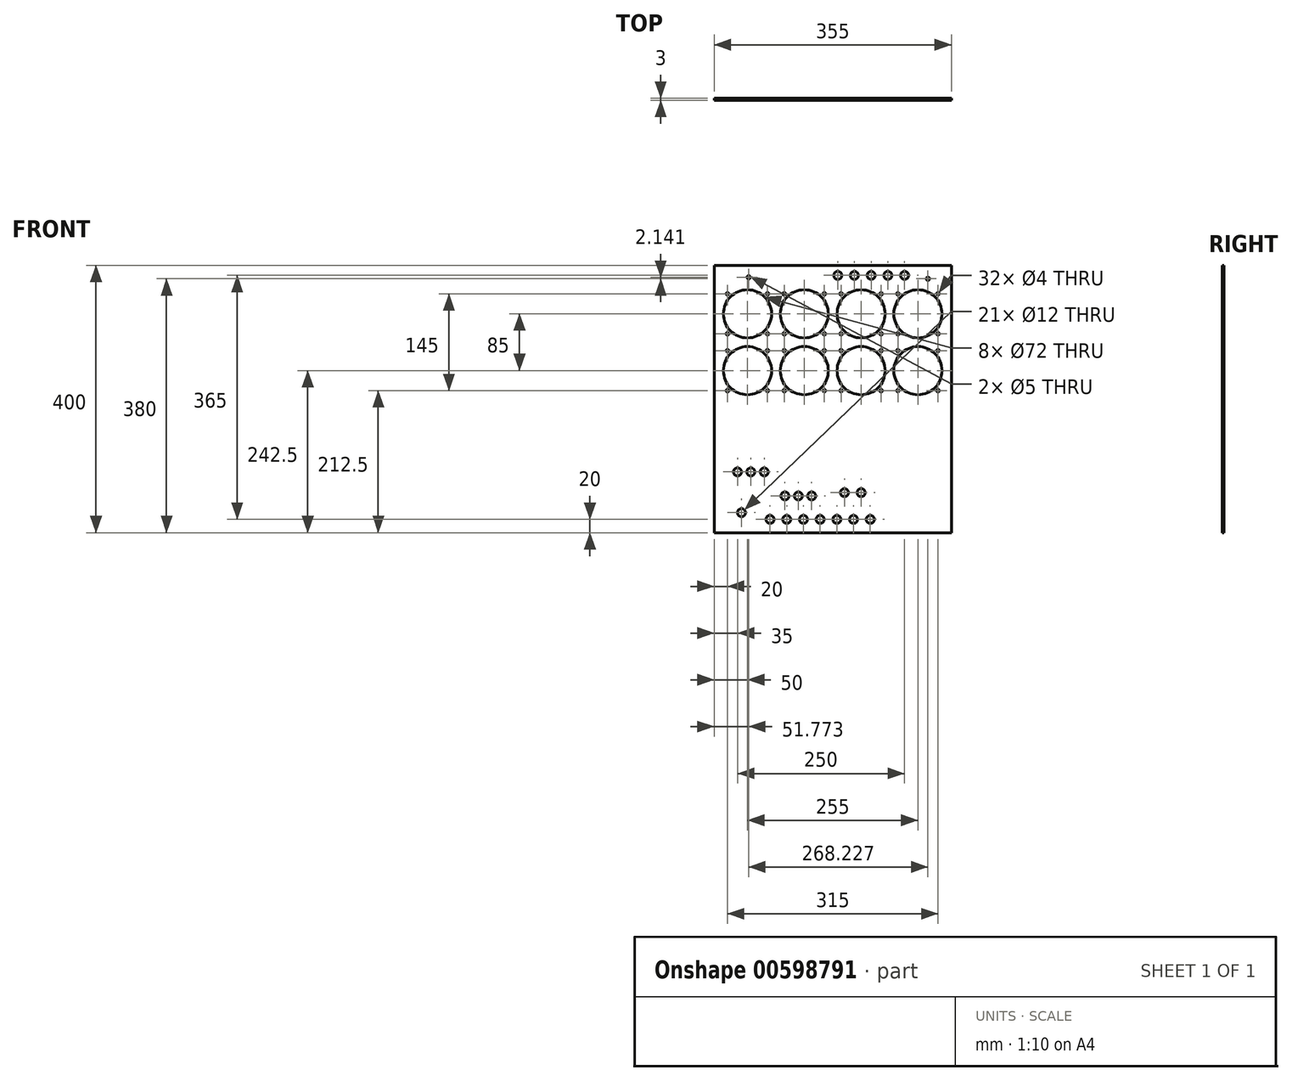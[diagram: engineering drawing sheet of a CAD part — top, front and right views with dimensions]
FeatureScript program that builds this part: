
annotation { "Feature Type Name" : "Feature", "Feature Type Description" : "" }
export const myFeature = defineFeature(function(context is Context, id is Id, definition is map)
    precondition{}
    {
        {
            var Q0;
            Q0=qCreatedBy(makeId("Front.planeOp"),FACE);
            var sketch = newSketch(context, id + "F0", { "sketchPlane" : qUnion([Q0])});
            skLineSegment(sketch, "E0.bottom", {"start": v(0, 0) * mm, "end": v(355, 0) * mm});
            skLineSegment(sketch, "E0.top", {"start": v(0, 400) * mm, "end": v(355, 400) * mm});
            skLineSegment(sketch, "E0.left", {"start": v(0, 0) * mm, "end": v(0, 400) * mm});
            skLineSegment(sketch, "E0.right", {"start": v(355, 0) * mm, "end": v(355, 400) * mm});
            skCircle(sketch, "E1", {"center": v(50, 327.5) * mm, "radius": 36 * mm});
            skCircle(sketch, "E2.0.1.0", {"center": v(50, 242.5) * mm, "radius": 36 * mm});
            skCircle(sketch, "E2.1.0.0", {"center": v(135, 327.5) * mm, "radius": 36 * mm});
            skCircle(sketch, "E2.1.1.0", {"center": v(135, 242.5) * mm, "radius": 36 * mm});
            skCircle(sketch, "E2.2.0.0", {"center": v(220, 327.5) * mm, "radius": 36 * mm});
            skCircle(sketch, "E2.2.1.0", {"center": v(220, 242.5) * mm, "radius": 36 * mm});
            skCircle(sketch, "E2.3.0.0", {"center": v(305, 327.5) * mm, "radius": 36 * mm});
            skCircle(sketch, "E2.3.1.0", {"center": v(305, 242.5) * mm, "radius": 36 * mm});
            skLineSegment(sketch, "E2.direction1", {"start": v(50, 327.5) * mm, "end": v(135, 327.5) * mm, "construction": true});
            skLineSegment(sketch, "E2.direction2", {"start": v(50, 327.5) * mm, "end": v(50, 242.5) * mm, "construction": true});
            skSolve(sketch);
        }
        {
            var Q0;
            Q0 = qSketchRegion(id + "F0", true);
            var Q1;
            Q1=makeQuery(id+"F0.imprint","IMPRINT",FACE,{"disambiguationData":[TD([[makeQuery(id+"F0.imprint","IMPRINT",EDGE,{"derivedFrom":sQuery(id+"F0.wireOp",EDGE,"E0.bottom")}),1.0]])]});
            extrude(context, id + "F1", {"entities" : qUnion([Q0, Q1]), "oppositeDirection" : true, "depth" : 3 * mm, "offsetDistance" : 25 * mm});
        }
        {
            var Q0;
            Q0=makeQuery(id+"F1.opExtrude","CAP_FACE",FACE,{"disambiguationData":[OSD([sQuery(id+"F0.wireOp",EDGE,"E0.bottom"),sQuery(id+"F0.wireOp",EDGE,"E0.top"),sQuery(id+"F0.wireOp",EDGE,"E0.left"),sQuery(id+"F0.wireOp",EDGE,"E0.right"),sQuery(id+"F0.wireOp",EDGE,"E1"),sQuery(id+"F0.wireOp",EDGE,"E2.0.1.0"),sQuery(id+"F0.wireOp",EDGE,"E2.1.0.0"),sQuery(id+"F0.wireOp",EDGE,"E2.1.1.0"),sQuery(id+"F0.wireOp",EDGE,"E2.2.0.0"),sQuery(id+"F0.wireOp",EDGE,"E2.2.1.0"),sQuery(id+"F0.wireOp",EDGE,"E2.3.0.0"),sQuery(id+"F0.wireOp",EDGE,"E2.3.1.0")])],"isStart":true});
            var sketch = newSketch(context, id + "F2", { "sketchPlane" : qUnion([Q0])});
            skCircle(sketch, "E3", {"center": v(20, 357.5) * mm, "radius": 2 * mm});
            skLineSegment(sketch, "E4", {"start": v(50, 327.5) * mm, "end": v(50, 382.4) * mm, "construction": true});
            skLineSegment(sketch, "E5", {"start": v(50, 327.5) * mm, "end": v(4.53, 327.5) * mm, "construction": true});
            skCircle(sketch, "E6.MirrorC", {"center": v(80, 357.5) * mm, "radius": 2 * mm});
            skCircle(sketch, "E7.MirrorC", {"center": v(80, 297.5) * mm, "radius": 2 * mm});
            skCircle(sketch, "E8.MirrorC", {"center": v(20, 297.5) * mm, "radius": 2 * mm});
            skCircle(sketch, "E9.0.1.0", {"center": v(80, 272.5) * mm, "radius": 2 * mm});
            skCircle(sketch, "E9.0.1.1", {"center": v(80, 212.5) * mm, "radius": 2 * mm});
            skCircle(sketch, "E9.0.1.2", {"center": v(20, 212.5) * mm, "radius": 2 * mm});
            skCircle(sketch, "E9.0.1.3", {"center": v(20, 272.5) * mm, "radius": 2 * mm});
            skCircle(sketch, "E9.1.0.0", {"center": v(165, 357.5) * mm, "radius": 2 * mm});
            skCircle(sketch, "E9.1.0.1", {"center": v(165, 297.5) * mm, "radius": 2 * mm});
            skCircle(sketch, "E9.1.0.2", {"center": v(105, 297.5) * mm, "radius": 2 * mm});
            skCircle(sketch, "E9.1.0.3", {"center": v(105, 357.5) * mm, "radius": 2 * mm});
            skCircle(sketch, "E9.1.1.0", {"center": v(165, 272.5) * mm, "radius": 2 * mm});
            skCircle(sketch, "E9.1.1.1", {"center": v(165, 212.5) * mm, "radius": 2 * mm});
            skCircle(sketch, "E9.1.1.2", {"center": v(105, 212.5) * mm, "radius": 2 * mm});
            skCircle(sketch, "E9.1.1.3", {"center": v(105, 272.5) * mm, "radius": 2 * mm});
            skCircle(sketch, "E9.2.0.0", {"center": v(250, 357.5) * mm, "radius": 2 * mm});
            skCircle(sketch, "E9.2.0.1", {"center": v(250, 297.5) * mm, "radius": 2 * mm});
            skCircle(sketch, "E9.2.0.2", {"center": v(190, 297.5) * mm, "radius": 2 * mm});
            skCircle(sketch, "E9.2.0.3", {"center": v(190, 357.5) * mm, "radius": 2 * mm});
            skCircle(sketch, "E9.2.1.0", {"center": v(250, 272.5) * mm, "radius": 2 * mm});
            skCircle(sketch, "E9.2.1.1", {"center": v(250, 212.5) * mm, "radius": 2 * mm});
            skCircle(sketch, "E9.2.1.2", {"center": v(190, 212.5) * mm, "radius": 2 * mm});
            skCircle(sketch, "E9.2.1.3", {"center": v(190, 272.5) * mm, "radius": 2 * mm});
            skCircle(sketch, "E9.3.0.0", {"center": v(335, 357.5) * mm, "radius": 2 * mm});
            skCircle(sketch, "E9.3.0.1", {"center": v(335, 297.5) * mm, "radius": 2 * mm});
            skCircle(sketch, "E9.3.0.2", {"center": v(275, 297.5) * mm, "radius": 2 * mm});
            skCircle(sketch, "E9.3.0.3", {"center": v(275, 357.5) * mm, "radius": 2 * mm});
            skCircle(sketch, "E9.3.1.0", {"center": v(335, 272.5) * mm, "radius": 2 * mm});
            skCircle(sketch, "E9.3.1.1", {"center": v(335, 212.5) * mm, "radius": 2 * mm});
            skCircle(sketch, "E9.3.1.2", {"center": v(275, 212.5) * mm, "radius": 2 * mm});
            skCircle(sketch, "E9.3.1.3", {"center": v(275, 272.5) * mm, "radius": 2 * mm});
            skLineSegment(sketch, "E9.direction1", {"start": v(80, 357.5) * mm, "end": v(165, 357.5) * mm, "construction": true});
            skLineSegment(sketch, "E9.direction2", {"start": v(80, 357.5) * mm, "end": v(80, 272.5) * mm, "construction": true});
            skSolve(sketch);
        }
        {
            var Q0;
            Q0 = qSketchRegion(id + "F2", true);
            extrude(context, id + "F3", {"entities" : qUnion([Q0]), "operationType" : NewBodyOperationType.REMOVE, "oppositeDirection" : true, "depth" : 3 * mm, "offsetDistance" : 25 * mm});
        }
        {
            var Q0;
            Q0=makeQuery(id+"F1.opExtrude","CAP_FACE",FACE,{"disambiguationData":[OSD([sQuery(id+"F0.wireOp",EDGE,"E0.bottom"),sQuery(id+"F0.wireOp",EDGE,"E0.top"),sQuery(id+"F0.wireOp",EDGE,"E0.left"),sQuery(id+"F0.wireOp",EDGE,"E0.right"),sQuery(id+"F0.wireOp",EDGE,"E1"),sQuery(id+"F0.wireOp",EDGE,"E2.0.1.0"),sQuery(id+"F0.wireOp",EDGE,"E2.1.0.0"),sQuery(id+"F0.wireOp",EDGE,"E2.1.1.0"),sQuery(id+"F0.wireOp",EDGE,"E2.2.0.0"),sQuery(id+"F0.wireOp",EDGE,"E2.2.1.0"),sQuery(id+"F0.wireOp",EDGE,"E2.3.0.0"),sQuery(id+"F0.wireOp",EDGE,"E2.3.1.0")])],"isStart":true});
            var sketch = newSketch(context, id + "F4", { "sketchPlane" : qUnion([Q0])});
            skCircle(sketch, "E10", {"center": v(35, 91) * mm, "radius": 6 * mm});
            skCircle(sketch, "E11.1.0.1", {"center": v(55, 91) * mm, "radius": 6 * mm});
            skCircle(sketch, "E11.2.0.1", {"center": v(75, 91) * mm, "radius": 6 * mm});
            skLineSegment(sketch, "E11.direction1", {"start": v(35, 91) * mm, "end": v(55, 91) * mm, "construction": true});
            skCircle(sketch, "E12", {"center": v(106, 55) * mm, "radius": 6 * mm});
            skCircle(sketch, "E13.1.0.0", {"center": v(126, 55) * mm, "radius": 6 * mm});
            skCircle(sketch, "E13.2.0.0", {"center": v(146, 55) * mm, "radius": 6 * mm});
            skLineSegment(sketch, "E13.direction1", {"start": v(106, 55) * mm, "end": v(126, 55) * mm, "construction": true});
            skCircle(sketch, "E14", {"center": v(41, 30) * mm, "radius": 6 * mm});
            skCircle(sketch, "E15", {"center": v(83.71, 20) * mm, "radius": 6 * mm});
            skCircle(sketch, "E16.1.0.0", {"center": v(108.71, 20) * mm, "radius": 6 * mm});
            skCircle(sketch, "E16.2.0.0", {"center": v(133.71, 20) * mm, "radius": 6 * mm});
            skCircle(sketch, "E16.3.0.0", {"center": v(158.71, 20) * mm, "radius": 6 * mm});
            skCircle(sketch, "E16.4.0.0", {"center": v(183.71, 20) * mm, "radius": 6 * mm});
            skCircle(sketch, "E16.5.0.0", {"center": v(208.71, 20) * mm, "radius": 6 * mm});
            skCircle(sketch, "E16.6.0.0", {"center": v(233.71, 20) * mm, "radius": 6 * mm});
            skLineSegment(sketch, "E16.direction1", {"start": v(83.71, 20) * mm, "end": v(108.71, 20) * mm, "construction": true});
            skCircle(sketch, "E17", {"center": v(195, 60) * mm, "radius": 6 * mm});
            skCircle(sketch, "E18.1.0.0", {"center": v(220, 60) * mm, "radius": 6 * mm});
            skLineSegment(sketch, "E18.direction1", {"start": v(195, 60) * mm, "end": v(220, 60) * mm, "construction": true});
            skCircle(sketch, "E19", {"center": v(185, 385) * mm, "radius": 6 * mm});
            skCircle(sketch, "E20.1.0.0", {"center": v(210, 385) * mm, "radius": 6 * mm});
            skCircle(sketch, "E20.2.0.0", {"center": v(235, 385) * mm, "radius": 6 * mm});
            skCircle(sketch, "E20.3.0.0", {"center": v(260, 385) * mm, "radius": 6 * mm});
            skCircle(sketch, "E20.4.0.0", {"center": v(285, 385) * mm, "radius": 6 * mm});
            skLineSegment(sketch, "E20.direction1", {"start": v(185, 385) * mm, "end": v(210, 385) * mm, "construction": true});
            skCircle(sketch, "E21", {"center": v(320, 380) * mm, "radius": 2.5 * mm});
            skCircle(sketch, "E22", {"center": v(51.77, 382.14) * mm, "radius": 2.5 * mm});
            skSolve(sketch);
        }
        {
            var Q0;
            Q0 = qSketchRegion(id + "F4", true);
            extrude(context, id + "F5", {"entities" : qUnion([Q0]), "operationType" : NewBodyOperationType.REMOVE, "oppositeDirection" : true, "depth" : 3 * mm, "offsetDistance" : 25 * mm});
        }
    });
